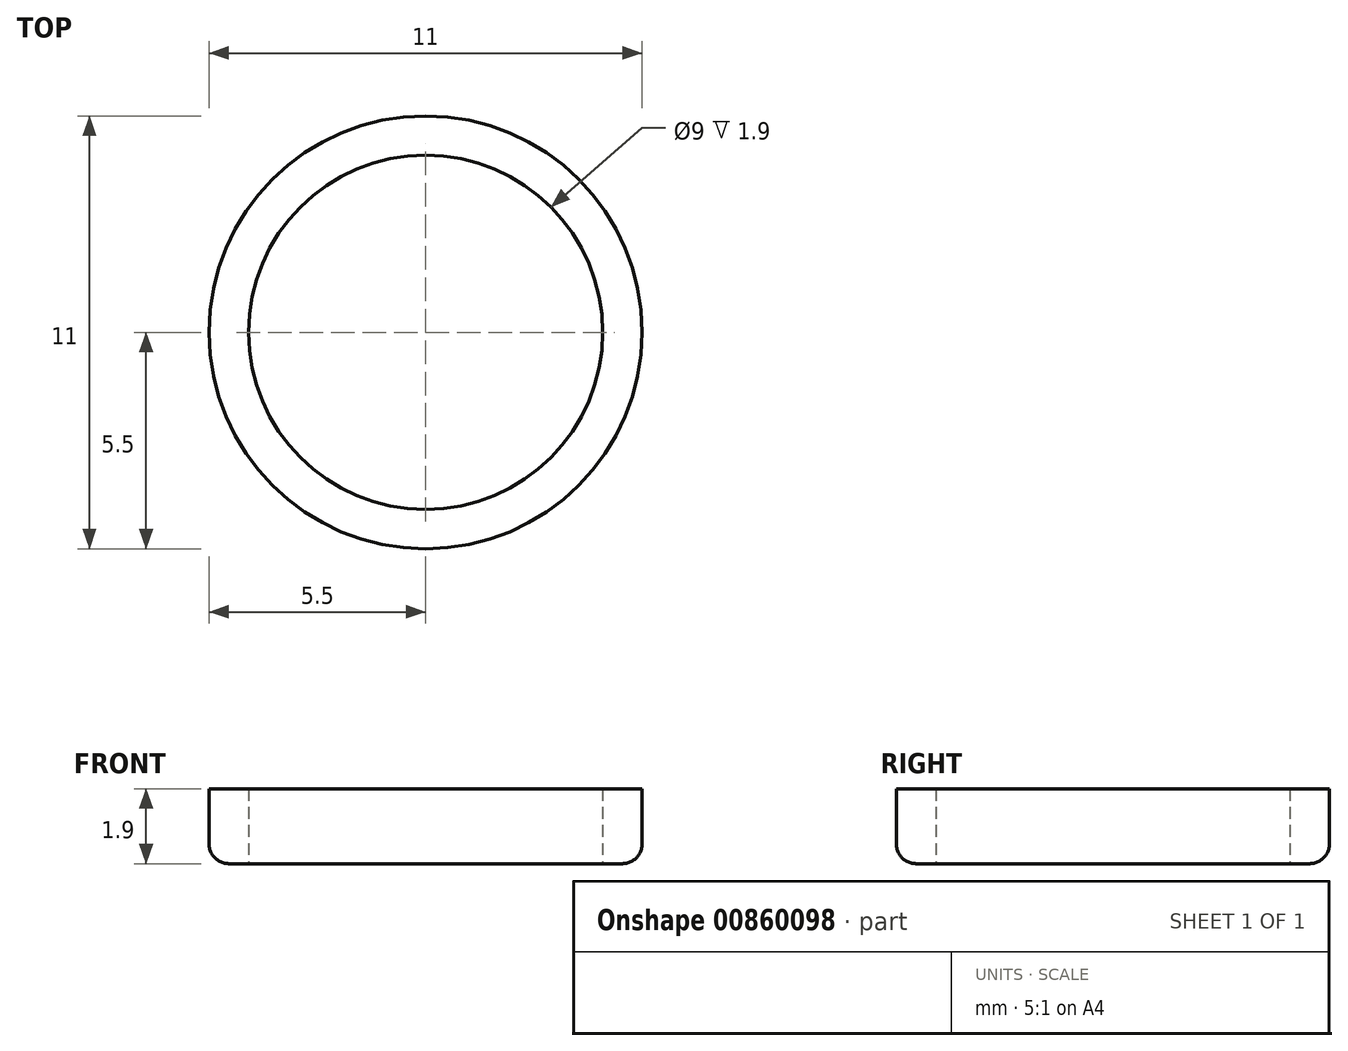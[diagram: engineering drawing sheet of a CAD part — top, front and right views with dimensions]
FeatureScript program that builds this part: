
annotation { "Feature Type Name" : "Feature", "Feature Type Description" : "" }
export const myFeature = defineFeature(function(context is Context, id is Id, definition is map)
    precondition{}
    {
        {
            var Q0;
            Q0=qCreatedBy(makeId("Top.planeOp"),FACE);
            var sketch = newSketch(context, id + "F0", { "sketchPlane" : qUnion([Q0])});
            skCircle(sketch, "E0", {"center": v(0, 0) * mm, "radius": 4.5 * mm});
            skCircle(sketch, "E1.0", {"center": v(0, 0) * mm, "radius": 5.5 * mm});
            skSolve(sketch);
        }
        {
            var Q0;
            Q0 = qSketchRegion(id + "F0", true);
            extrude(context, id + "F1", {"entities" : qUnion([Q0]), "depth" : 1.9 * mm, "offsetDistance" : 25 * mm});
        }
        {
            var Q0;
            Q0=makeQuery(id+"F1.opExtrude","CAP_EDGE",EDGE,{"disambiguationData":[OSD([sQuery(id+"F0.wireOp",EDGE,"E1.0")])],"isStart":true});
            fillet(context, id + "F2", {"entities" : qUnion([Q0]), "radius" : 0.5 * mm, "tangentPropagation" : true, "allowEdgeOverflow" : false});
        }
    });
